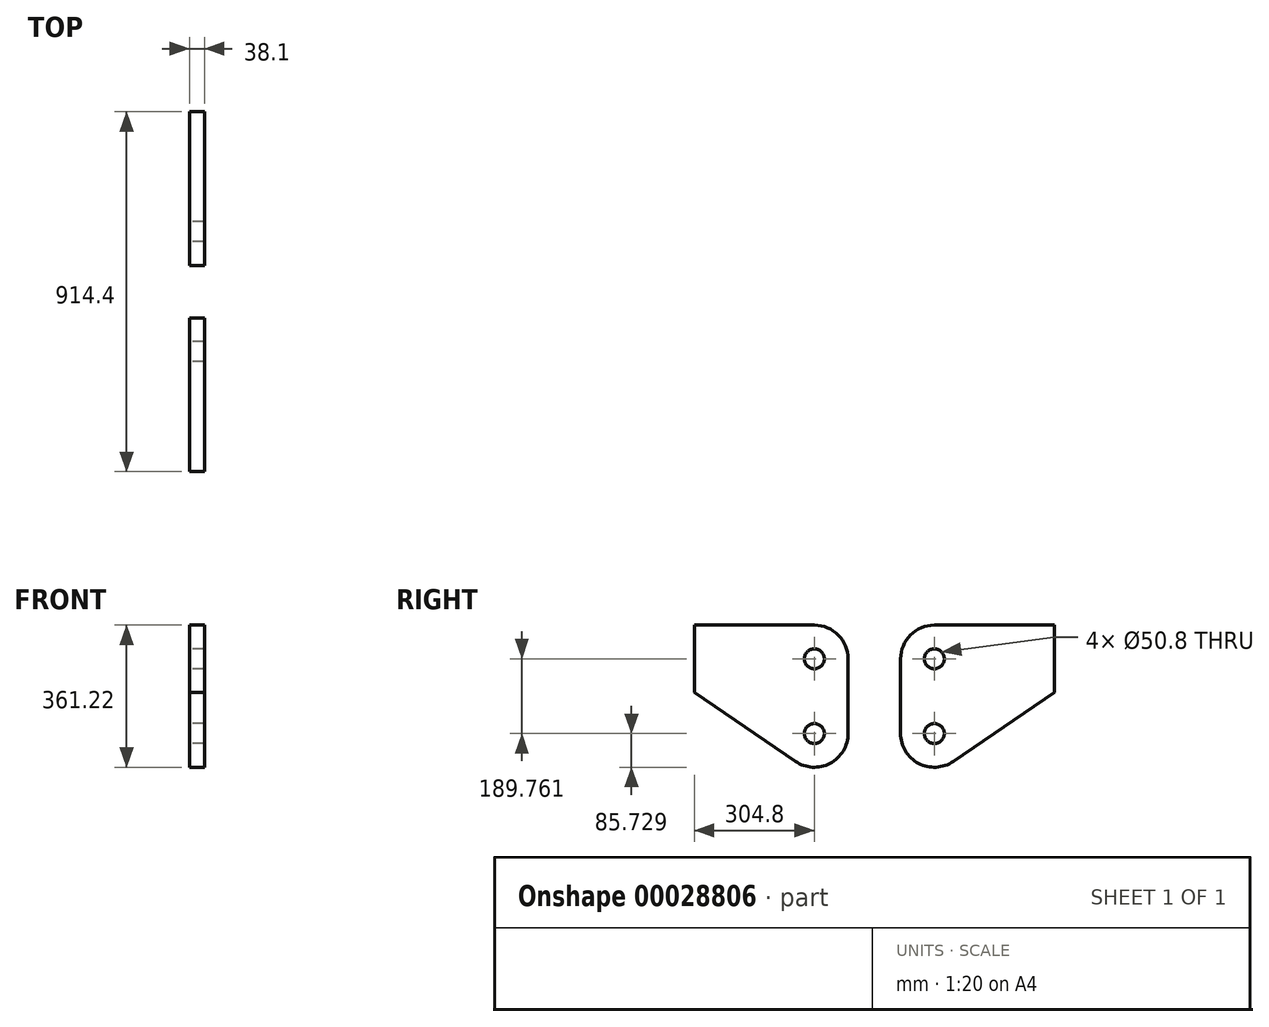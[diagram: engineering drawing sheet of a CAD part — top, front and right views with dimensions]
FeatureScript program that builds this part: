
annotation { "Feature Type Name" : "Feature", "Feature Type Description" : "" }
export const myFeature = defineFeature(function(context is Context, id is Id, definition is map)
    precondition{}
    {
        {
            var Q0;
            Q0=qCreatedBy(makeId("Right.planeOp"),FACE);
            var sketch = newSketch(context, id + "F0", { "sketchPlane" : qUnion([Q0])});
            skCircle(sketch, "E0", {"center": v(0, 0) * mm, "radius": 25.4 * mm});
            skLineSegment(sketch, "E1", {"start": v(304.8, 85.73) * mm, "end": v(304.8, -85.72) * mm});
            skCircle(sketch, "E2", {"center": v(0, -189.76) * mm, "radius": 25.4 * mm});
            skPoint(sketch, "E3.orphan", {"position": v(0, -82.55) * mm});
            skArc(sketch, "E4", {"start": v(0, 85.73) * mm, "mid": v(-60.62, 60.62) * mm, "end": v(-85.73, 0) * mm});
            skLineSegment(sketch, "E5", {"start": v(0, 85.73) * mm, "end": v(304.8, 85.73) * mm});
            skArc(sketch, "E6", {"start": v(-85.73, -189.76) * mm, "mid": v(-40.06, -265.55) * mm, "end": v(48.29, -260.6) * mm});
            skLineSegment(sketch, "E7", {"start": v(-85.73, 0) * mm, "end": v(-85.73, -189.76) * mm});
            skLineSegment(sketch, "E8", {"start": v(304.8, -85.73) * mm, "end": v(48.29, -260.6) * mm});
            skSolve(sketch);
        }
        {
            var Q0;
            Q0=makeQuery(id+"F0.imprint","IMPRINT",FACE,{"disambiguationData":[TD([[makeQuery(id+"F0.imprint","IMPRINT",EDGE,{"derivedFrom":sQuery(id+"F0.wireOp",EDGE,"E0")}),-1.0]])]});
            extrude(context, id + "F1", {"entities" : qUnion([Q0]), "depth" : 38.1 * mm});
        }
        {
            var Q0;
            Q0=qCreatedBy(makeId("Front.planeOp"),FACE);
            cPlane(context, id + "F2", {"entities" : qUnion([Q0]), "cplaneType" : CPlaneType.OFFSET, "offset" : 152.4 * mm, "width" : 152.4 * mm, "height" : 152.4 * mm});
        }
        {
            var Q0;
            Q0=makeQuery(id+"F1.opExtrude","SWEPT_BODY",BODY,{"disambiguationData":[OSD([sQuery(id+"F0.wireOp",EDGE,"E0"),sQuery(id+"F0.wireOp",EDGE,"3bbac358-53a1-41e3-850f-8c677b92bad7"),sQuery(id+"F0.wireOp",EDGE,"8599c6ac-ccbf-40c1-958b-3beec8ea1a1d"),sQuery(id+"F0.wireOp",EDGE,"E1"),sQuery(id+"F0.wireOp",EDGE,"E2"),sQuery(id+"F0.wireOp",EDGE,"a179b785-ad26-4931-8f29-ca237679fad9"),sQuery(id+"F0.wireOp",EDGE,"4514a489-14d6-47dc-aa1a-d91a431bee49"),sQuery(id+"F0.wireOp",EDGE,"5008d965-1a48-49af-8b88-580fb5d2ad9f")])]});
            var Q1;
            Q1=qCreatedBy(id+"F2.planeOp",FACE);
            mirror(context, id + "F3", {"entities" : qUnion([Q0]), "mirrorPlane" : qUnion([Q1])});
        }
    });
